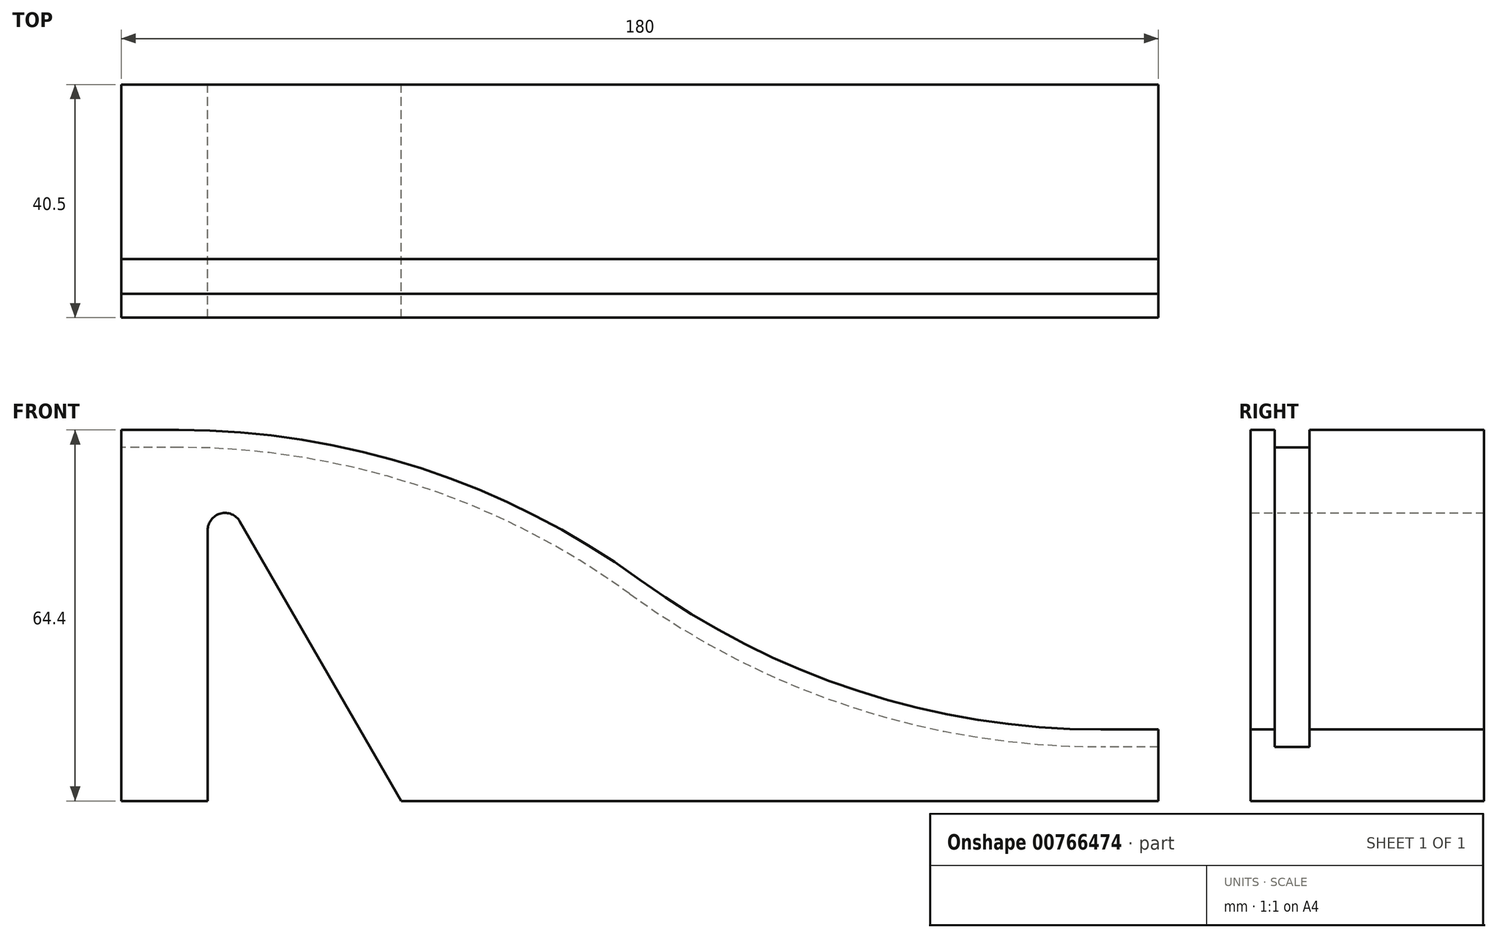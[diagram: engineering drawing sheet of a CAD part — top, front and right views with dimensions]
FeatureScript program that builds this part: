
annotation { "Feature Type Name" : "Feature", "Feature Type Description" : "" }
export const myFeature = defineFeature(function(context is Context, id is Id, definition is map)
    precondition{}
    {
        {
            var Q0;
            Q0=qCreatedBy(makeId("Front.planeOp"),FACE);
            var sketch = newSketch(context, id + "F0", { "sketchPlane" : qUnion([Q0])});
            skLineSegment(sketch, "E0", {"start": v(0, 64.4) * mm, "end": v(0, 0) * mm});
            skLineSegment(sketch, "E1", {"start": v(0, 0) * mm, "end": v(15, 0) * mm});
            skLineSegment(sketch, "E2", {"start": v(180, 0) * mm, "end": v(180, 12.4) * mm});
            skLineSegment(sketch, "E3", {"start": v(180, 12.4) * mm, "end": v(170, 12.4) * mm});
            skLineSegment(sketch, "E4", {"start": v(0, 64.4) * mm, "end": v(10, 64.4) * mm});
            skArc(sketch, "E5", {"start": v(90, 38.4) * mm, "mid": v(52.06, 57.74) * mm, "end": v(10, 64.4) * mm});
            skArc(sketch, "E6", {"start": v(90, 38.4) * mm, "mid": v(127.94, 19.06) * mm, "end": v(170, 12.4) * mm});
            skLineSegment(sketch, "E7", {"start": v(15, 0) * mm, "end": v(15, 47) * mm});
            skLineSegment(sketch, "E8", {"start": v(20.6, 48.5) * mm, "end": v(48.6, 0) * mm});
            skPoint(sketch, "E9.visualSharp", {"position": v(15, 58.2) * mm});
            skArc(sketch, "E9.filletArc", {"start": v(20.6, 48.5) * mm, "mid": v(17.22, 49.9) * mm, "end": v(15, 47) * mm});
            skLineSegment(sketch, "E10.trimOffspring", {"start": v(48.6, 0) * mm, "end": v(180, 0) * mm});
            skSolve(sketch);
        }
        {
            var Q0;
            Q0=makeQuery(id+"F0.imprint","IMPRINT",FACE,{"disambiguationData":[TD([[makeQuery(id+"F0.imprint","IMPRINT",EDGE,{"derivedFrom":sQuery(id+"F0.wireOp",EDGE,"E0")}),1.0]])]});
            extrude(context, id + "F1", {"entities" : qUnion([Q0]), "endBound" : BoundingType.SYMMETRIC, "depth" : 40.5 * mm, "offsetDistance" : 25 * mm});
        }
        {
            var Q0;
            Q0=makeQuery(id+"F1.opExtrude","SWEPT_FACE",FACE,{"disambiguationData":[OSD([sQuery(id+"F0.wireOp",EDGE,"E2")])]});
            var sketch = newSketch(context, id + "F2", { "sketchPlane" : qUnion([Q0])});
            skLineSegment(sketch, "E11.0", {"start": v(-16.07, 12.4) * mm, "end": v(-10.08, 12.4) * mm});
            skLineSegment(sketch, "E12", {"start": v(-16.07, 12.4) * mm, "end": v(-16.07, 9.4) * mm});
            skLineSegment(sketch, "E13", {"start": v(-16.07, 9.4) * mm, "end": v(-10.07, 9.4) * mm});
            skLineSegment(sketch, "E14", {"start": v(-10.07, 9.4) * mm, "end": v(-10.08, 12.4) * mm});
            skPoint(sketch, "E15.orphan", {"position": v(20.25, 12.4) * mm});
            skPoint(sketch, "E16.orphan", {"position": v(-20.25, 12.4) * mm});
            skSolve(sketch);
        }
        {
            var Q0;
            Q0=makeQuery(id+"F2.imprint","IMPRINT",FACE,{"disambiguationData":[TD([[makeQuery(id+"F2.imprint","IMPRINT",EDGE,{"derivedFrom":sQuery(id+"F2.wireOp",EDGE,"E11.0")}),-1.0]])]});
            var Q1;
            Q1=sQuery(id+"F0.wireOp",EDGE,"E3");
            var Q2;
            Q2=sQuery(id+"F0.wireOp",EDGE,"E6");
            var Q3;
            Q3=sQuery(id+"F0.wireOp",EDGE,"E5");
            var Q4;
            Q4=sQuery(id+"F0.wireOp",EDGE,"E4");
            sweep(context, id + "F3", {"operationType" : NewBodyOperationType.REMOVE, "profiles" : qUnion([Q0]), "path" : qUnion([Q1, Q2, Q3, Q4])});
        }
    });
